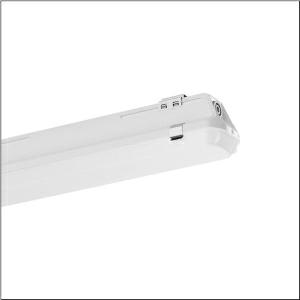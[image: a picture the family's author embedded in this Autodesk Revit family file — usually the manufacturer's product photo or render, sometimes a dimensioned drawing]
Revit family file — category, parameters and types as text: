
# Revit family: monsun_r__21_51fb10dl447j3h_07a2
name_source: partatom
category: Lighting Fixtures
units: mm (PartAtom-declared; Revit-internal decimal feet)

## family parameters
Cut with Voids When Loaded = No
Host = Face
Light Source = No
Part Type = Normal
Room Calculation Point = No
Round Connector Dimension = Use Diameter
Shared = No

## types (1)
- --- (1 x LED, 850 lm, 4.5 W, 4000K)
    Apparent Load = 5 VA
    CIE Flux Codes = 46 76 93 94 100
    Color Rendering = 80
    Color Temperature = 4000K
    Default Elevation = 1800 mm
    Description = Monsun® 21, damp-proof luminaire, chain hanger, primary optical cover: enclosure, of PMMA, light emission: direct distribution, primary light characteristic: symmetric, installation type: suspended mounting, surface-mounted, horizontal mounting, vertical mounting, LED, rated luminous flux: 4.330lm, luminous efficacy: 140lm/W, light colour: 840, colour temperature: 4000K, control gear: ECG DALI, with terminal, 5-pole, max. 2.5mm², mains connection: 220..240V, AC, 50/60Hz, rated input power: 31W, control gear: single battery element, battery: NiCd, 4,5Ah, mains connection: 230V, housing, of glass-fibre reinforced plastic, uncoated, bright grey, incl. chain hanger, length: 1.299mm, width: 90mm, height: 88mm, clip for enclosure, of stainless steel (V2A), ceiling mounting element, of stainless steel (V2A), chain hanger, of stainless steel (V2A), protection rating (complete): IP66, insulation class (complete): insulation class I (protective earthing), certification: CE, UKCA, protection symbol: D, impact resistance: IK04, permissible operating ambient temperature: +5..+25°C, standard: EN 50419, EN 60598-2-1, corresponds to IFS (International Featured Standards) requirements for safety and quality in the food industry, for indoor or canopied outdoor use, no direct snow, no direct sun, no direct rain, contact your sales advisor before using the luminaires in applications with unclear chemical exposure, large temperature fluctuations or condensation-forming humidity, LABS conformity tested according to VDMA 24364:2018-05, packaging unit: 1 piece
    Height = 88 mm
    Lamp = 1 x LED
    Lamp Light Flux = 850 lm
    Lamp Power = 4.5 W
    Lamp count = 1
    Length = 1299 mm
    Luminous efficacy = 189 lm/W
    Manufacturer = Siteco
    ModVariant = No
    Model = 51FB10DL447J3H
    Mounting Place = Ceiling
    Mounting Type = Surface mounted
    Number of Poles = 1
    OnlyDefault = Yes
    Power Factor = 1
    Product Name = Monsun® 21
    Product group = damp-proof luminaire
    ProductGroupID = 300
    Protection Class = Protection class I
    Protection Degree = IP 66
    RLX_Detail_Level = 1
    RLX_Emergency_Light_Flux = 0 lm
    RLX_Emergency_Type = 0
    RLX_Emergency_Type_DB = No
    RlxData = <blob elided: 93697 chars, md5=284a9a1f>
    Socket = socket
    Standby Power = 0 W
    System Light Flux = 850 lm
    System Power = 5 W
    Type Comments = : 3 h
    Type Image = l_1006717.jpg
    URL = http://relux.com
    VarID = @adj_074885
    Voltage = 0 V
    Weight = 0.00 kg
    Width = 90 mm

## geometry (parser evidence)
native form markers: Blend x4, Sweep x13
no freeform markers — native parametric forms only
